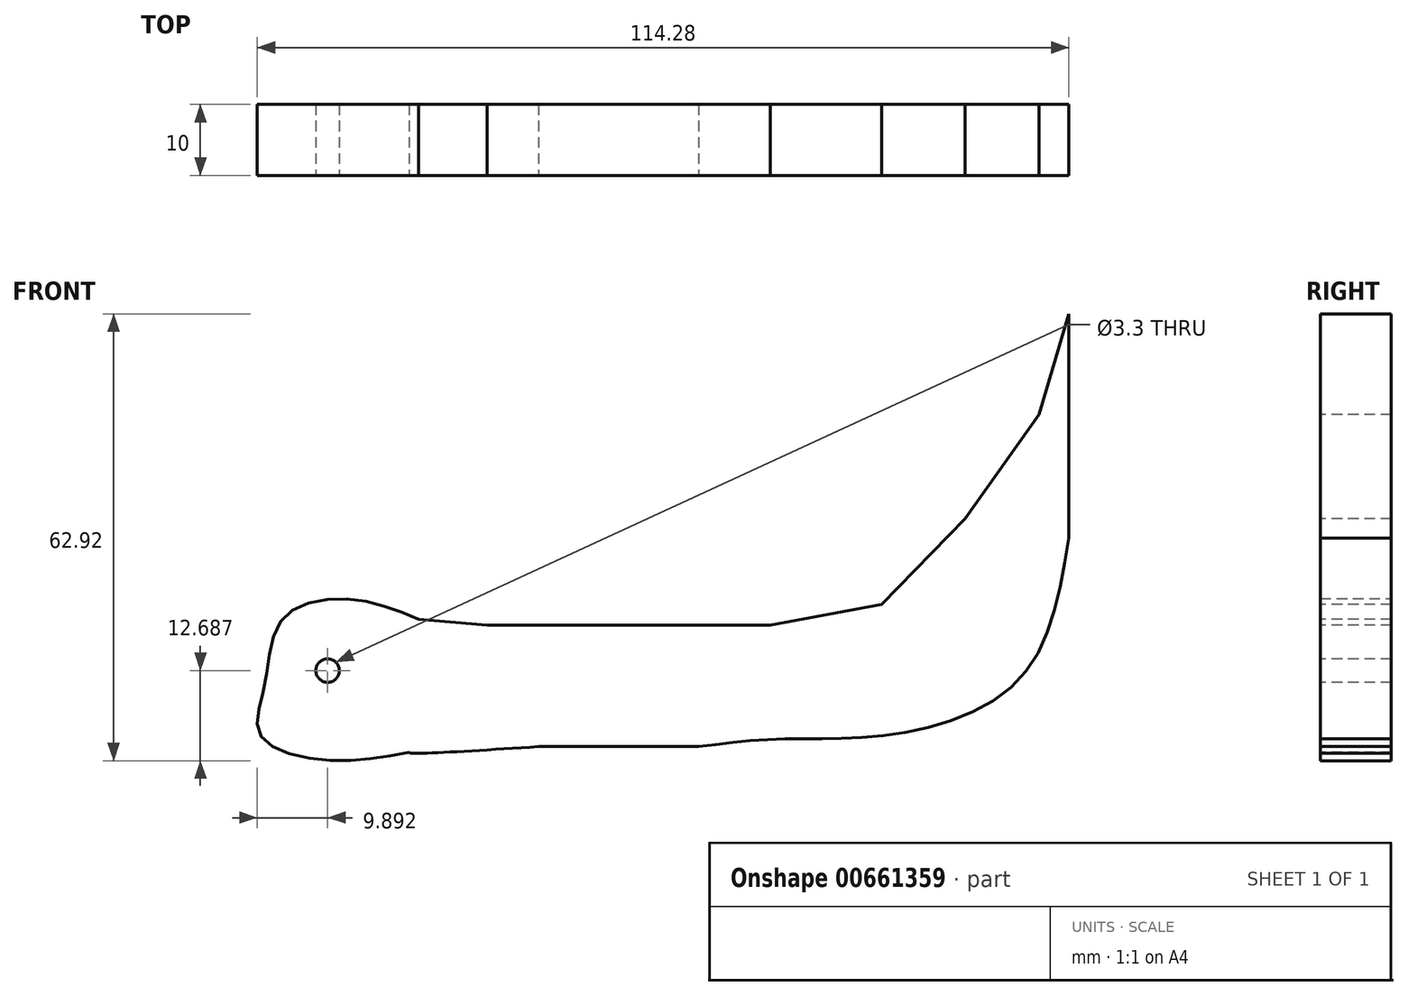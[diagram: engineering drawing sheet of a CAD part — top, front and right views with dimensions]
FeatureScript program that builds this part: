
annotation { "Feature Type Name" : "Feature", "Feature Type Description" : "" }
export const myFeature = defineFeature(function(context is Context, id is Id, definition is map)
    precondition{}
    {
        {
            var Q0;
            Q0=qCreatedBy(makeId("Front.planeOp"),FACE);
            var sketch = newSketch(context, id + "F0", { "sketchPlane" : qUnion([Q0])});
            skLineSegment(sketch, "E0", {"start": v(-20.1, 54.3) * mm, "end": v(-10.47, 53.44) * mm});
            skLineSegment(sketch, "E1", {"start": v(-10.47, 53.44) * mm, "end": v(-1.82, 53.44) * mm});
            skLineSegment(sketch, "E2", {"start": v(-1.82, 53.44) * mm, "end": v(20.27, 53.44) * mm});
            skLineSegment(sketch, "E3", {"start": v(20.27, 53.44) * mm, "end": v(29.41, 53.44) * mm});
            skLineSegment(sketch, "E4", {"start": v(29.41, 53.44) * mm, "end": v(45.08, 56.36) * mm});
            skLineSegment(sketch, "E5", {"start": v(45.08, 56.36) * mm, "end": v(56.83, 68.43) * mm});
            skLineSegment(sketch, "E6", {"start": v(56.83, 68.43) * mm, "end": v(67.28, 83.12) * mm});
            skFitSpline(sketch, "E7", {"points": [v(67.28, 83.12) * mm, v(71.44, 97.28) * mm], "startDerivative": vector(4.16, 14.16) * mm, "endDerivative": vector(4.16, 14.16) * mm});
            skFitSpline(sketch, "E8", {"points": [v(71.44, 97.28) * mm, v(71.44, 83.12) * mm], "startDerivative": vector(0, -14.16) * mm, "endDerivative": vector(0, -14.16) * mm});
            skFitSpline(sketch, "E9", {"points": [v(71.44, 83.12) * mm, v(71.44, 65.71) * mm], "startDerivative": vector(0, -17.4) * mm, "endDerivative": vector(0, -17.4) * mm});
            skFitSpline(sketch, "E10", {"points": [v(71.44, 65.71) * mm, v(64.58, 45.95) * mm, v(46.19, 38) * mm, v(31.1, 37.44) * mm, v(19.29, 36.35) * mm], "startDerivative": vector(-12.83, -79.95) * mm, "endDerivative": vector(-55.16, -6.99) * mm});
            skFitSpline(sketch, "E11", {"points": [v(19.29, 36.35) * mm, v(-3.22, 36.35) * mm], "startDerivative": vector(-22.5, 0) * mm, "endDerivative": vector(-22.5, 0) * mm});
            skFitSpline(sketch, "E12", {"points": [v(-3.22, 36.35) * mm, v(-21.46, 35.5) * mm, v(-21.46, 35.56) * mm], "startDerivative": vector(-28.4, -1.83) * mm, "endDerivative": vector(0.51, 1.14) * mm});
            skFitSpline(sketch, "E13", {"points": [v(-20.1, 54.3) * mm, v(-30.18, 57.15) * mm, v(-39.3, 54.3) * mm, v(-41.82, 44.92) * mm, v(-42.4, 37.93) * mm, v(-33.28, 34.44) * mm, v(-21.46, 35.56) * mm], "startDerivative": vector(-55.92, 22.7) * mm, "endDerivative": vector(61.98, 11.63) * mm});
            skSolve(sketch);
        }
        {
            var Q0;
            Q0 = qSketchRegion(id + "F0", true);
            extrude(context, id + "F1", {"entities" : qUnion([Q0]), "oppositeDirection" : true, "depth" : 10 * mm, "offsetDistance" : 25 * mm});
        }
        {
            var Q0;
            Q0=makeQuery(id+"F1.opExtrude","CAP_FACE",FACE,{"disambiguationData":[OSD([sQuery(id+"F0.wireOp",EDGE,"E0"),sQuery(id+"F0.wireOp",EDGE,"E1"),sQuery(id+"F0.wireOp",EDGE,"E2"),sQuery(id+"F0.wireOp",EDGE,"E3"),sQuery(id+"F0.wireOp",EDGE,"E4"),sQuery(id+"F0.wireOp",EDGE,"E5"),sQuery(id+"F0.wireOp",EDGE,"E6"),sQuery(id+"F0.wireOp",EDGE,"E7"),sQuery(id+"F0.wireOp",EDGE,"E8"),sQuery(id+"F0.wireOp",EDGE,"E9"),sQuery(id+"F0.wireOp",EDGE,"E10"),sQuery(id+"F0.wireOp",EDGE,"E11"),sQuery(id+"F0.wireOp",EDGE,"E12"),sQuery(id+"F0.wireOp",EDGE,"E13")])],"isStart":true});
            var sketch = newSketch(context, id + "F2", { "sketchPlane" : qUnion([Q0])});
            skCircle(sketch, "E14", {"center": v(-32.95, 47.05) * mm, "radius": 3.5 * mm});
            skSolve(sketch);
        }
        {
            var Q0;
            Q0=sQuery(id+"F2.wireOp",VERTEX,"E14.center");
            var Q1;
            Q1=makeQuery(id+"F1.opExtrude","SWEPT_BODY",BODY,{"disambiguationData":[OSD([sQuery(id+"F0.wireOp",EDGE,"E0"),sQuery(id+"F0.wireOp",EDGE,"E1"),sQuery(id+"F0.wireOp",EDGE,"E2"),sQuery(id+"F0.wireOp",EDGE,"E3"),sQuery(id+"F0.wireOp",EDGE,"E4"),sQuery(id+"F0.wireOp",EDGE,"E5"),sQuery(id+"F0.wireOp",EDGE,"E6"),sQuery(id+"F0.wireOp",EDGE,"E7"),sQuery(id+"F0.wireOp",EDGE,"E8"),sQuery(id+"F0.wireOp",EDGE,"E9"),sQuery(id+"F0.wireOp",EDGE,"E10"),sQuery(id+"F0.wireOp",EDGE,"E11"),sQuery(id+"F0.wireOp",EDGE,"E12"),sQuery(id+"F0.wireOp",EDGE,"E13")])]});
            hole(context, id + "F3", {"style" : HoleStyle.SIMPLE, "endStyle" : HoleEndStyle.THROUGH, "standardTappedOrClearance" : lookupTablePath({ "standard" : "ISO", "fit" : "Normal", "size" : "M3", "type" : "Clearance" }), "standardBlindInLast" : lookupTablePath({ "fit" : "Standard", "standard" : "ISO", "size" : "M3", "type" : "Clearance" }), "holeDiameter" : 3.3 * mm, "majorDiameter" : 5 * mm, "isTappedThrough" : true, "tappedDepth" : 12 * mm, "tapClearance" : 3, "startFromSketch" : true, "locations" : qUnion([Q0]), "scope" : qUnion([Q1])});
        }
    });
